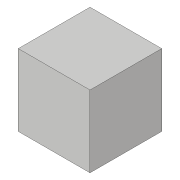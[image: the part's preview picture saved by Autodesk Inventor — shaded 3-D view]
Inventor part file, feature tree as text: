
AUTODESK INVENTOR PART (.ipt)
format: ipt  version: 2018 (Build 220112000, 112)  size: 72,192 bytes
history: native  units: in
note: dims shown in document units (in); Inventor stores cm internally (conversion verified against a paired STEP export)
features: extrude x1, sketch x1
ambient origin geometry x8: Origin, YZ Plane, XZ Plane, XY Plane, X Axis, Y Axis, Z Axis, Center Point
bodies: Solid1 (feature_tree)
feature tree (2):
  extrude  "Extrusion1"  Depth=6.0in
  sketch  "Sketch1"  dims[d0=6.0in d1=6.0in d2=6.0in d3=0.0in]
